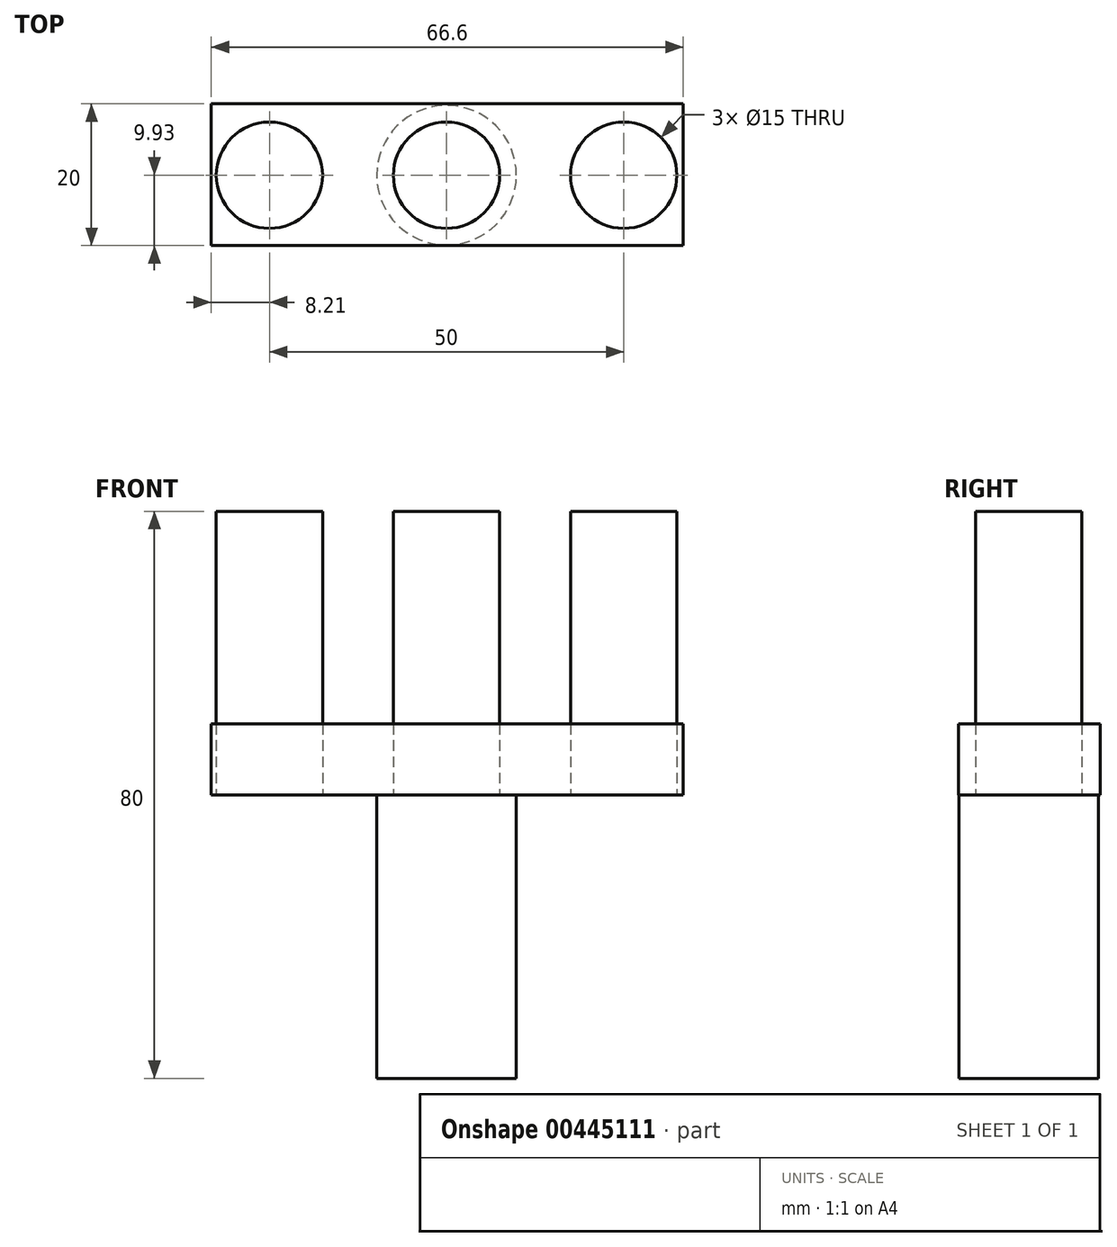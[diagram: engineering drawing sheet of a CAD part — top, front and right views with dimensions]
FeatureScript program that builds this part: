
annotation { "Feature Type Name" : "Feature", "Feature Type Description" : "" }
export const myFeature = defineFeature(function(context is Context, id is Id, definition is map)
    precondition{}
    {
        {
            var Q0;
            Q0=qCreatedBy(makeId("Top.planeOp"),FACE);
            var sketch = newSketch(context, id + "F0", { "sketchPlane" : qUnion([Q0])});
            skLineSegment(sketch, "E0.bottom", {"start": v(-33.2, -9.93) * mm, "end": v(33.39, -9.93) * mm});
            skLineSegment(sketch, "E0.top", {"start": v(-33.2, 10.07) * mm, "end": v(33.39, 10.07) * mm});
            skLineSegment(sketch, "E0.left", {"start": v(-33.2, -9.93) * mm, "end": v(-33.2, 10.07) * mm});
            skLineSegment(sketch, "E0.right", {"start": v(33.39, -9.93) * mm, "end": v(33.39, 10.07) * mm});
            skCircle(sketch, "E1", {"center": v(0, 0) * mm, "radius": 7.5 * mm});
            skLineSegment(sketch, "E2", {"start": v(7.5, 0) * mm, "end": v(17.5, 0) * mm});
            skLineSegment(sketch, "E3", {"start": v(17.5, 0) * mm, "end": v(25, 0) * mm});
            skCircle(sketch, "E4", {"center": v(25, 0) * mm, "radius": 7.5 * mm});
            skLineSegment(sketch, "E5", {"start": v(-7.5, 0) * mm, "end": v(-25, 0) * mm});
            skCircle(sketch, "E6", {"center": v(-25, 0) * mm, "radius": 7.5 * mm});
            skSolve(sketch);
        }
        {
            var Q0;
            {var subQ0=sQuery(id+"F0.wireOp",EDGE,"E1");var subQ1=makeQuery(id+"F0.imprint","IMPRINT",VERTEX,{"disambiguationData":[OD(0.0)],"derivedFrom":subQ0});Q0=makeQuery(id+"F0.imprint","IMPRINT",FACE,{"disambiguationData":[TD([[makeQuery(id+"F0.imprint","IMPRINT",EDGE,{"disambiguationData":[TD([[subQ1,-1.0]])],"derivedFrom":subQ0}),1.0]])]});}
            var Q1;
            Q1=makeQuery(id+"F0.imprint","IMPRINT",FACE,{"disambiguationData":[TD([[makeQuery(id+"F0.imprint","IMPRINT",EDGE,{"derivedFrom":sQuery(id+"F0.wireOp",EDGE,"E4")}),1.0]])]});
            var Q2;
            Q2=makeQuery(id+"F0.imprint","IMPRINT",FACE,{"disambiguationData":[TD([[makeQuery(id+"F0.imprint","IMPRINT",EDGE,{"derivedFrom":sQuery(id+"F0.wireOp",EDGE,"E6")}),1.0]])]});
            extrude(context, id + "F1", {"entities" : qUnion([Q0, Q1, Q2]), "depth" : 40 * mm});
        }
        {
            var Q0;
            Q0 = qSketchRegion(id + "F0", true);
            extrude(context, id + "F2", {"entities" : qUnion([Q0]), "depth" : 10 * mm});
        }
        {
            var Q0;
            Q0=qCreatedBy(makeId("Top.planeOp"),FACE);
            var sketch = newSketch(context, id + "F3", { "sketchPlane" : qUnion([Q0])});
            skCircle(sketch, "E7", {"center": v(0, 0) * mm, "radius": 9.85 * mm});
            skSolve(sketch);
        }
        {
            var Q0;
            Q0 = qSketchRegion(id + "F3", true);
            extrude(context, id + "F4", {"entities" : qUnion([Q0]), "oppositeDirection" : true, "depth" : 40 * mm});
        }
    });
